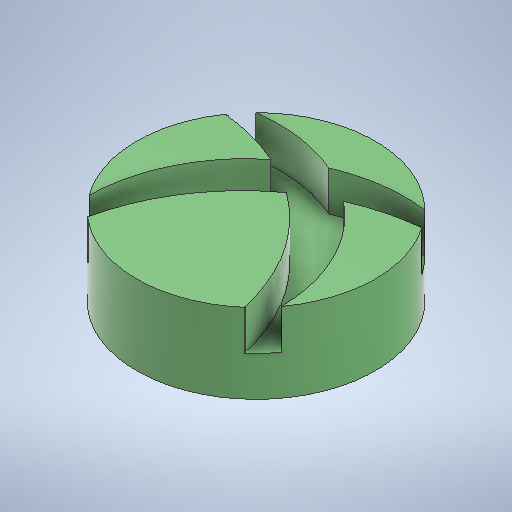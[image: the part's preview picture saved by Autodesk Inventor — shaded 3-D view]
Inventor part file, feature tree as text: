
AUTODESK INVENTOR PART (.ipt)
format: ipt  version: 2025 (Build 290162000, 162)  size: 317,952 bytes
history: native  units: mm
features: extrude x4, sketch x4, other x1
ambient origin geometry x8: Origin, YZ Plane, XZ Plane, XY Plane, X Axis, Y Axis, Z Axis, Center Point
bodies: Body1 (feature_tree)
feature tree (9):
  other  "Sólido1"
  extrude  "Extrusão1"  Depth=10.0mm TaperAngle=0.0deg
  extrude  "Extrusão2"  Depth=10.0mm TaperAngle=0.0deg
  extrude  "Extrusão3"  [1 undecoded]
  extrude  "Extrusão4"  [1 undecoded]
  sketch  "Esboço1"  dims[d1=20.0mm d2=0.0mm d11=10.0mm d12=0.0mm]
  sketch  "Esboço2"  dims[d13=10.0mm d14=0.0mm d15=10.0mm d16=0.0mm]
  sketch  "Esboço3"
  sketch  "Esboço4"
note: 2 required parameter values undecoded (feature->parameter linkage not recoverable at this tier; creation-order binding heuristic only, values carry confidence <= 0.55)
